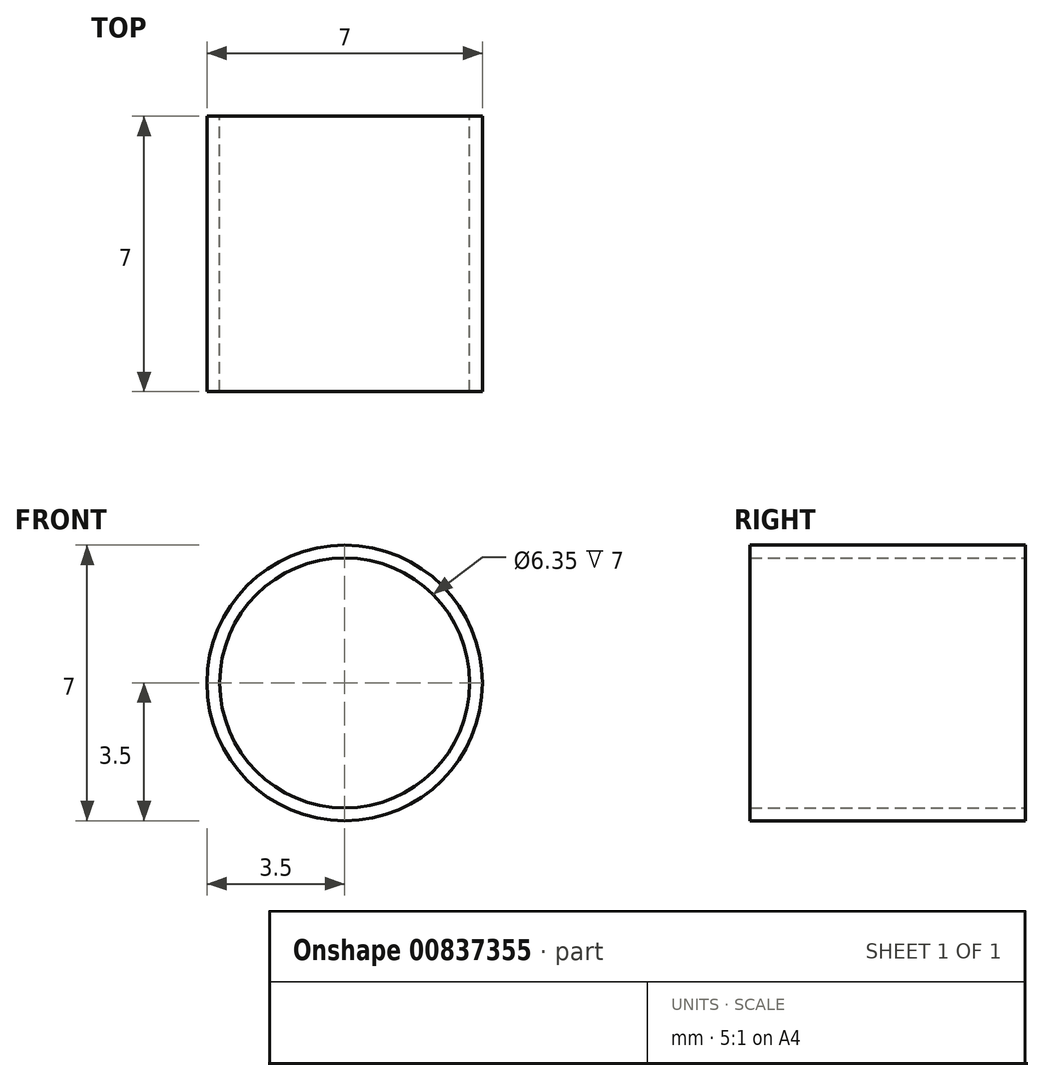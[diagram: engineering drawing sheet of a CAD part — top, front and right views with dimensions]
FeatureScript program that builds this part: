
annotation { "Feature Type Name" : "Feature", "Feature Type Description" : "" }
export const myFeature = defineFeature(function(context is Context, id is Id, definition is map)
    precondition{}
    {
        {
            var Q0;
            Q0=qCreatedBy(makeId("Front.planeOp"),FACE);
            var sketch = newSketch(context, id + "F0", { "sketchPlane" : qUnion([Q0])});
            skCircle(sketch, "E0", {"center": v(0, 0) * mm, "radius": 3.5 * mm});
            skCircle(sketch, "E1", {"center": v(0, 0) * mm, "radius": 3.18 * mm});
            skSolve(sketch);
        }
        {
            var Q0;
            Q0=makeQuery(id+"F0.imprint","IMPRINT",FACE,{"disambiguationData":[TD([[makeQuery(id+"F0.imprint","IMPRINT",EDGE,{"derivedFrom":sQuery(id+"F0.wireOp",EDGE,"E0")}),1.0]])]});
            extrude(context, id + "F1", {"entities" : qUnion([Q0]), "depth" : 7 * mm, "offsetDistance" : 25 * mm});
        }
    });
